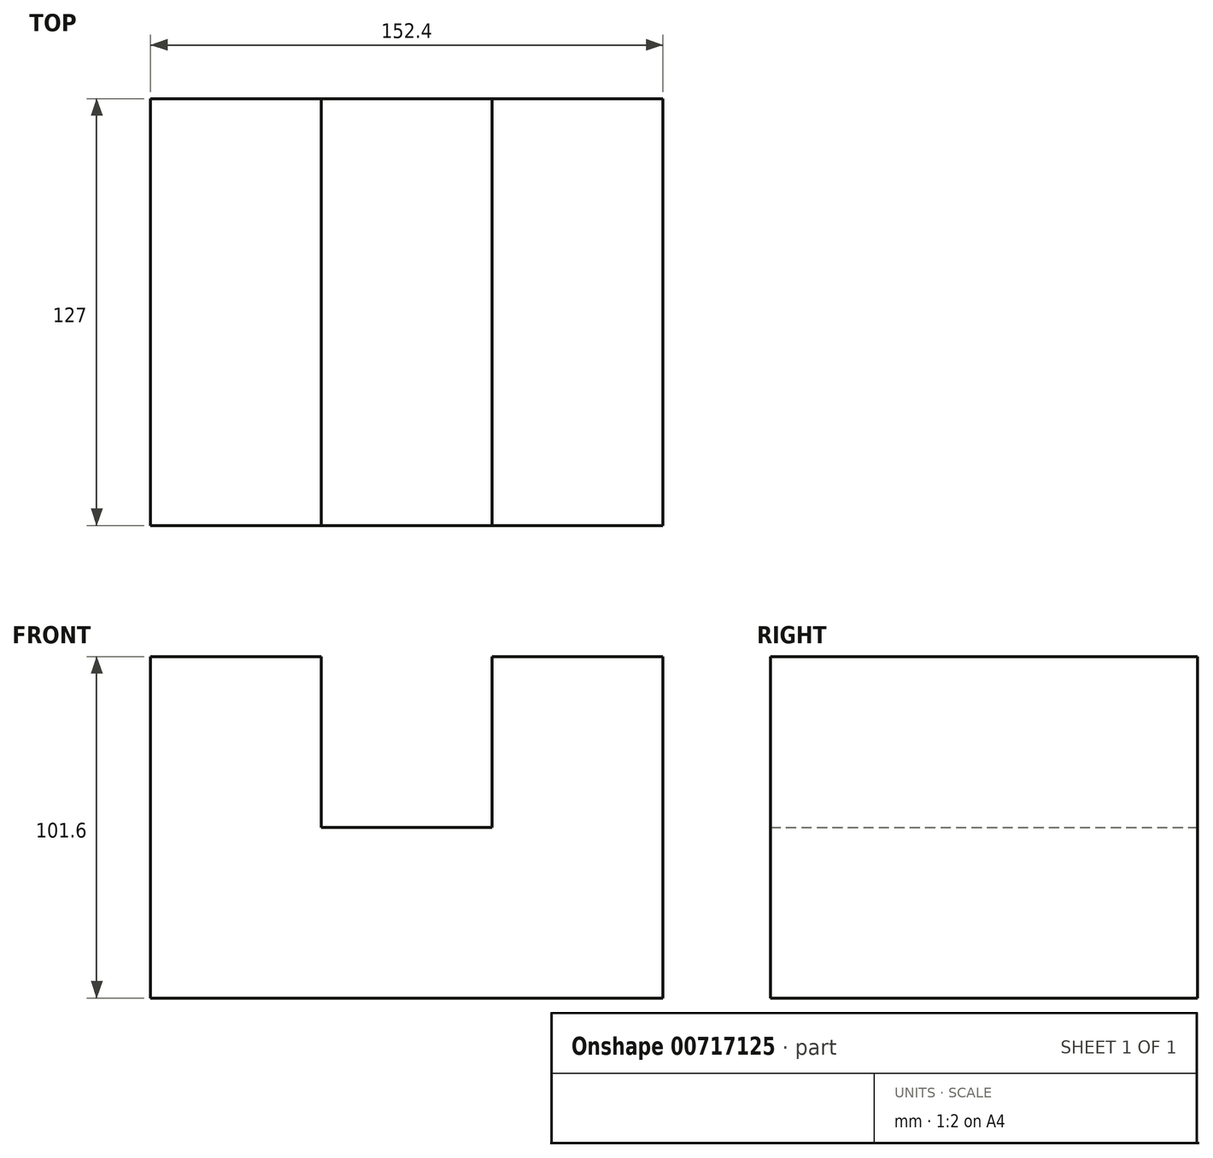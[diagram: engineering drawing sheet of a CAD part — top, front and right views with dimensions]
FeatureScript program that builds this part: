
annotation { "Feature Type Name" : "Feature", "Feature Type Description" : "" }
export const myFeature = defineFeature(function(context is Context, id is Id, definition is map)
    precondition{}
    {
        {
            var Q0;
            Q0=qCreatedBy(makeId("Front.planeOp"),FACE);
            var sketch = newSketch(context, id + "F0", { "sketchPlane" : qUnion([Q0])});
            skLineSegment(sketch, "E0", {"start": v(-76.28, -27.31) * mm, "end": v(76.12, -27.31) * mm});
            skLineSegment(sketch, "E1", {"start": v(76.12, -27.31) * mm, "end": v(76.12, 74.29) * mm});
            skLineSegment(sketch, "E2", {"start": v(76.12, 74.29) * mm, "end": v(25.32, 74.29) * mm});
            skLineSegment(sketch, "E3", {"start": v(25.32, 74.29) * mm, "end": v(25.32, 23.49) * mm});
            skLineSegment(sketch, "E4", {"start": v(25.32, 23.49) * mm, "end": v(-25.48, 23.49) * mm});
            skLineSegment(sketch, "E5", {"start": v(-25.48, 23.49) * mm, "end": v(-25.48, 74.29) * mm});
            skLineSegment(sketch, "E6", {"start": v(-25.48, 74.29) * mm, "end": v(-76.28, 74.29) * mm});
            skLineSegment(sketch, "E7", {"start": v(-76.28, 74.29) * mm, "end": v(-76.28, -27.31) * mm});
            skSolve(sketch);
        }
        {
            var Q0;
            Q0 = qSketchRegion(id + "F0", true);
            extrude(context, id + "F1", {"entities" : qUnion([Q0]), "depth" : 127 * mm, "offsetDistance" : 25.4 * mm});
        }
    });
